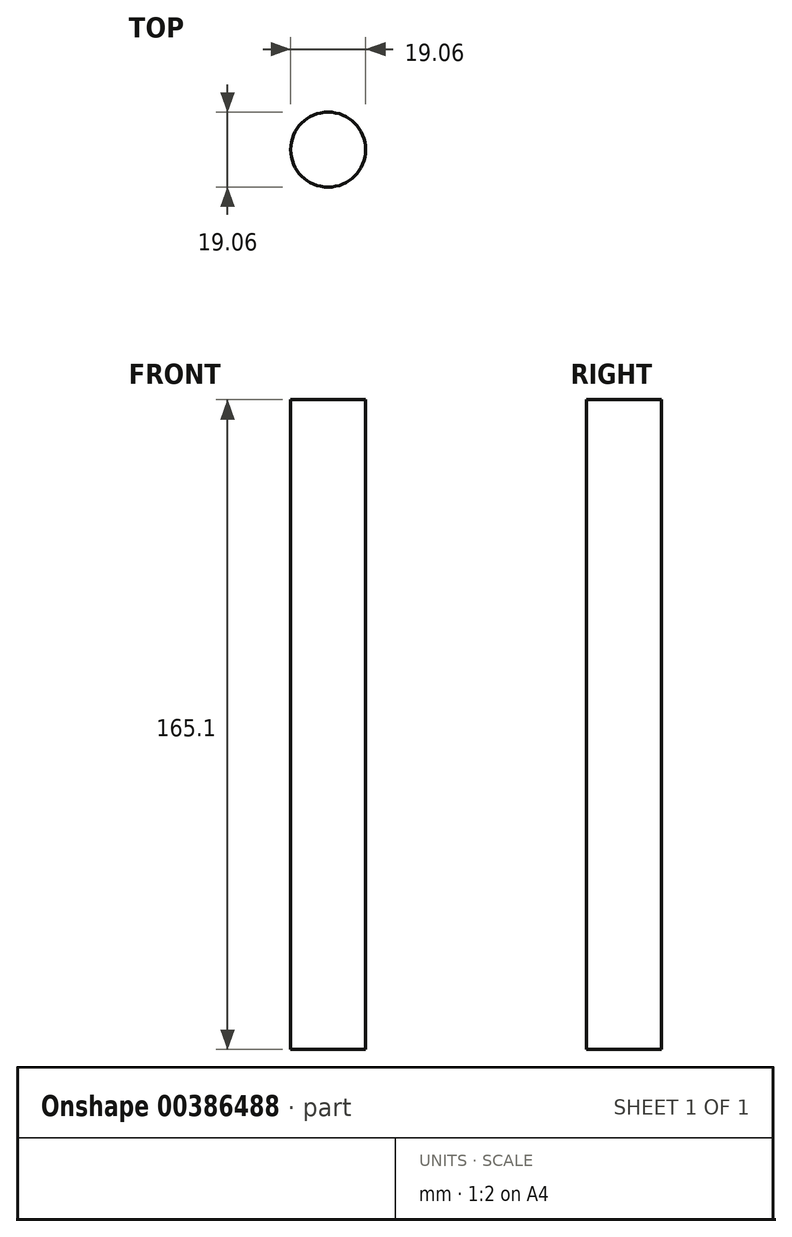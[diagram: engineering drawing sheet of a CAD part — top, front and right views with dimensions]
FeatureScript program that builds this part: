
annotation { "Feature Type Name" : "Feature", "Feature Type Description" : "" }
export const myFeature = defineFeature(function(context is Context, id is Id, definition is map)
    precondition{}
    {
        {
            var Q0;
            Q0=qCreatedBy(makeId("Top.planeOp"),FACE);
            var sketch = newSketch(context, id + "F0", { "sketchPlane" : qUnion([Q0])});
            skCircle(sketch, "E0", {"center": v(0, 0) * mm, "radius": 9.53 * mm});
            skSolve(sketch);
        }
        {
            var Q0;
            Q0=makeQuery(id+"F0.imprint","IMPRINT",FACE,{"disambiguationData":[TD([[makeQuery(id+"F0.imprint","IMPRINT",EDGE,{"derivedFrom":sQuery(id+"F0.wireOp",EDGE,"E0")}),1.0]])]});
            extrude(context, id + "F1", {"entities" : qUnion([Q0]), "depth" : 165.1 * mm});
        }
    });
